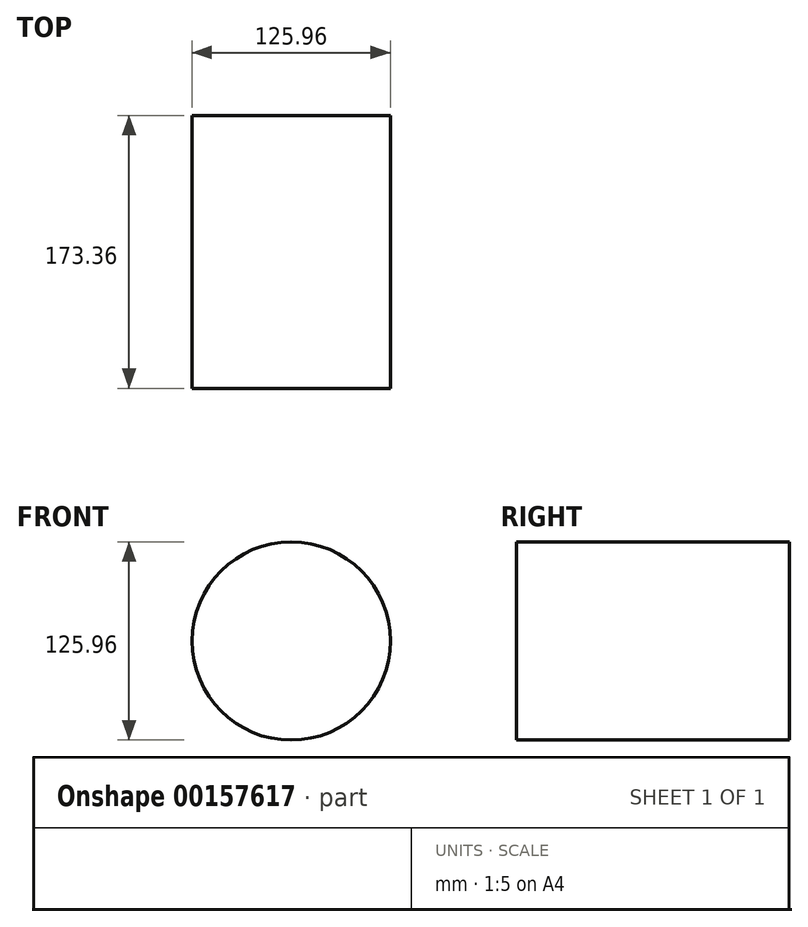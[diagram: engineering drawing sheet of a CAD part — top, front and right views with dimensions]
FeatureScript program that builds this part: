
annotation { "Feature Type Name" : "Feature", "Feature Type Description" : "" }
export const myFeature = defineFeature(function(context is Context, id is Id, definition is map)
    precondition{}
    {
        {
            var Q0;
            Q0=qCreatedBy(makeId("Front.planeOp"),FACE);
            var sketch = newSketch(context, id + "F0", { "sketchPlane" : qUnion([Q0])});
            skCircle(sketch, "E0", {"center": v(-51.95, 19.58) * mm, "radius": 62.98 * mm});
            skSolve(sketch);
        }
        {
            var Q0;
            Q0=makeQuery(id+"F0.imprint","IMPRINT",FACE,{"disambiguationData":[TD([[makeQuery(id+"F0.imprint","IMPRINT",EDGE,{"derivedFrom":sQuery(id+"F0.wireOp",EDGE,"E0")}),1.0]])]});
            extrude(context, id + "F1", {"entities" : qUnion([Q0]), "depth" : 173.35 * mm});
        }
    });
